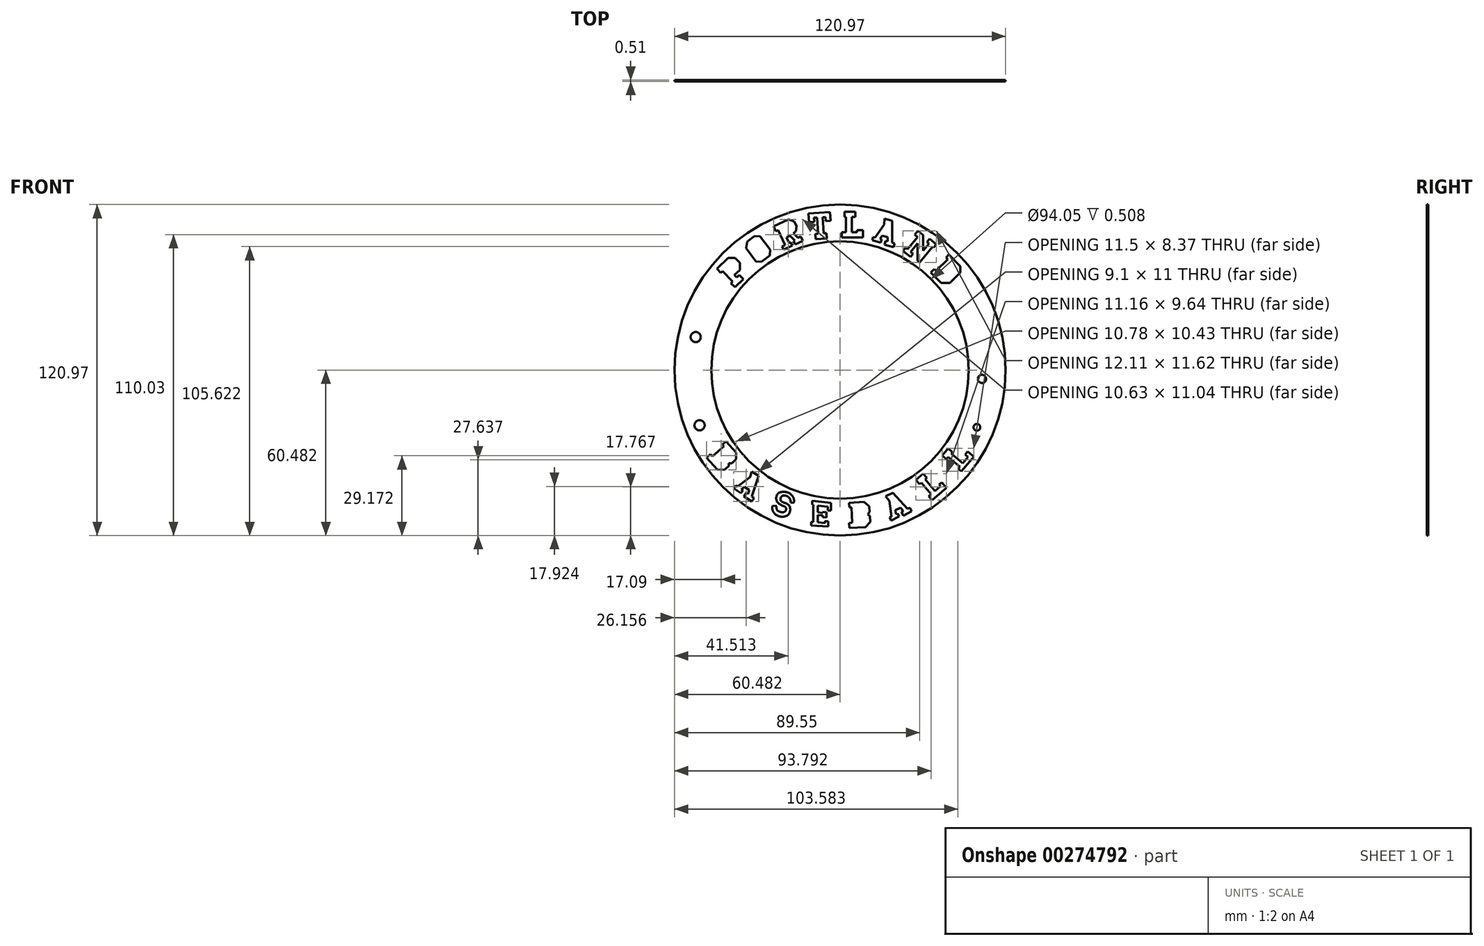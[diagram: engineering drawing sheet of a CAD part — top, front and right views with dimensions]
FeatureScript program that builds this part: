
annotation { "Feature Type Name" : "Feature", "Feature Type Description" : "" }
export const myFeature = defineFeature(function(context is Context, id is Id, definition is map)
    precondition{}
    {
        {
            var Q0;
            Q0=qCreatedBy(makeId("Front.planeOp"),FACE);
            var sketch = newSketch(context, id + "F0", { "sketchPlane" : qUnion([Q0])});
            skLineSegment(sketch, "E0", {"start": v(-46.28, 38.08) * mm, "end": v(-44.82, 36.56) * mm});
            skLineSegment(sketch, "E1", {"start": v(-44.82, 36.56) * mm, "end": v(-44.15, 37.2) * mm});
            skLineSegment(sketch, "E2", {"start": v(-44.15, 37.2) * mm, "end": v(-40.48, 33.42) * mm});
            skLineSegment(sketch, "E3", {"start": v(-40.48, 33.42) * mm, "end": v(-41.1, 32.81) * mm});
            skLineSegment(sketch, "E4", {"start": v(-41.1, 32.81) * mm, "end": v(-39.7, 31.36) * mm});
            skLineSegment(sketch, "E5", {"start": v(-39.7, 31.36) * mm, "end": v(-36.66, 34.3) * mm});
            skLineSegment(sketch, "E6", {"start": v(-36.66, 34.3) * mm, "end": v(-38.08, 35.77) * mm});
            skLineSegment(sketch, "E7", {"start": v(-38.08, 35.77) * mm, "end": v(-38.98, 34.9) * mm});
            skLineSegment(sketch, "E8", {"start": v(-38.98, 34.9) * mm, "end": v(-39.84, 35.8) * mm});
            skLineSegment(sketch, "E9", {"start": v(-39.84, 35.8) * mm, "end": v(-37.93, 37.66) * mm});
            skLineSegment(sketch, "E10", {"start": v(-37.93, 37.66) * mm, "end": v(-37.93, 40.3) * mm});
            skLineSegment(sketch, "E11", {"start": v(-37.93, 40.3) * mm, "end": v(-39.65, 42.08) * mm});
            skLineSegment(sketch, "E12", {"start": v(-46.28, 38.08) * mm, "end": v(-42.2, 42.04) * mm});
            skLineSegment(sketch, "E13", {"start": v(-42.2, 42.04) * mm, "end": v(-39.65, 42.08) * mm});
            skLineSegment(sketch, "E14", {"start": v(-35.23, 47.96) * mm, "end": v(-32.52, 50.01) * mm});
            skLineSegment(sketch, "E15", {"start": v(-32.52, 50.01) * mm, "end": v(-30.46, 49.88) * mm});
            skLineSegment(sketch, "E16", {"start": v(-30.46, 49.88) * mm, "end": v(-26.84, 45.1) * mm});
            skLineSegment(sketch, "E17", {"start": v(-26.84, 45.1) * mm, "end": v(-26.99, 42.91) * mm});
            skLineSegment(sketch, "E18", {"start": v(-26.99, 42.91) * mm, "end": v(-29.94, 40.67) * mm});
            skLineSegment(sketch, "E19", {"start": v(-29.94, 40.67) * mm, "end": v(-31.98, 40.8) * mm});
            skLineSegment(sketch, "E20", {"start": v(-31.98, 40.8) * mm, "end": v(-35.6, 45.6) * mm});
            skLineSegment(sketch, "E21", {"start": v(-35.6, 45.6) * mm, "end": v(-35.23, 47.96) * mm});
            skLineSegment(sketch, "E22", {"start": v(-25.56, 53.6) * mm, "end": v(-20.1, 56.13) * mm});
            skLineSegment(sketch, "E23", {"start": v(-20.1, 56.13) * mm, "end": v(-18.1, 55.45) * mm});
            skLineSegment(sketch, "E24", {"start": v(-18.1, 55.45) * mm, "end": v(-17.14, 53.74) * mm});
            skLineSegment(sketch, "E25", {"start": v(-17.14, 53.74) * mm, "end": v(-17.4, 51.8) * mm});
            skLineSegment(sketch, "E26", {"start": v(-17.4, 51.8) * mm, "end": v(-18.33, 51.12) * mm});
            skLineSegment(sketch, "E27", {"start": v(-18.33, 51.12) * mm, "end": v(-16.65, 49.44) * mm});
            skLineSegment(sketch, "E28", {"start": v(-16.65, 49.44) * mm, "end": v(-15.66, 49.9) * mm});
            skLineSegment(sketch, "E29", {"start": v(-15.66, 49.9) * mm, "end": v(-14.93, 48.34) * mm});
            skLineSegment(sketch, "E30", {"start": v(-14.93, 48.34) * mm, "end": v(-17.73, 47.04) * mm});
            skLineSegment(sketch, "E31", {"start": v(-17.73, 47.04) * mm, "end": v(-18.26, 48.19) * mm});
            skLineSegment(sketch, "E32", {"start": v(-18.26, 48.19) * mm, "end": v(-17.84, 48.38) * mm});
            skLineSegment(sketch, "E33", {"start": v(-17.84, 48.38) * mm, "end": v(-19.58, 50.13) * mm});
            skLineSegment(sketch, "E34", {"start": v(-19.58, 50.13) * mm, "end": v(-20.86, 49.53) * mm});
            skLineSegment(sketch, "E35", {"start": v(-20.86, 49.53) * mm, "end": v(-19.97, 47.61) * mm});
            skLineSegment(sketch, "E36", {"start": v(-19.24, 47.73) * mm, "end": v(-19.88, 47.43) * mm});
            skLineSegment(sketch, "E37", {"start": v(-19.97, 47.61) * mm, "end": v(-19.88, 47.43) * mm});
            skLineSegment(sketch, "E38", {"start": v(-19.24, 47.73) * mm, "end": v(-18.7, 46.58) * mm});
            skLineSegment(sketch, "E39", {"start": v(-18.7, 46.58) * mm, "end": v(-21.91, 45.1) * mm});
            skLineSegment(sketch, "E40", {"start": v(-21.91, 45.1) * mm, "end": v(-22.45, 46.24) * mm});
            skLineSegment(sketch, "E41", {"start": v(-21.35, 46.75) * mm, "end": v(-23.88, 52.19) * mm});
            skLineSegment(sketch, "E42", {"start": v(-23.88, 52.19) * mm, "end": v(-24.72, 51.8) * mm});
            skLineSegment(sketch, "E43.trimOffspring", {"start": v(-21.35, 46.75) * mm, "end": v(-22.45, 46.24) * mm});
            skLineSegment(sketch, "E44", {"start": v(-25.56, 53.6) * mm, "end": v(-24.72, 51.8) * mm});
            skLineSegment(sketch, "E45", {"start": v(-5.45, 58.78) * mm, "end": v(-12.82, 58.3) * mm});
            skLineSegment(sketch, "E46", {"start": v(-12.82, 58.3) * mm, "end": v(-12.6, 55.1) * mm});
            skLineSegment(sketch, "E47", {"start": v(-10.7, 55.23) * mm, "end": v(-10.75, 55.96) * mm});
            skLineSegment(sketch, "E48", {"start": v(-9.68, 56.03) * mm, "end": v(-9.34, 50.88) * mm});
            skLineSegment(sketch, "E49", {"start": v(-9.34, 50.88) * mm, "end": v(-10.33, 50.81) * mm});
            skLineSegment(sketch, "E50", {"start": v(-10.33, 50.81) * mm, "end": v(-10.2, 48.93) * mm});
            skLineSegment(sketch, "E51", {"start": v(-10.2, 48.93) * mm, "end": v(-6.13, 49.2) * mm});
            skLineSegment(sketch, "E52", {"start": v(-7.6, 56.16) * mm, "end": v(-7.26, 51.04) * mm});
            skLineSegment(sketch, "E53", {"start": v(-6.13, 49.2) * mm, "end": v(-6.25, 51.08) * mm});
            skLineSegment(sketch, "E54", {"start": v(-5.45, 58.78) * mm, "end": v(-4.98, 58.8) * mm});
            skLineSegment(sketch, "E55", {"start": v(-4.98, 58.8) * mm, "end": v(-4.77, 55.62) * mm});
            skLineSegment(sketch, "E56.trimOffspring", {"start": v(-6.54, 55.5) * mm, "end": v(-6.59, 56.23) * mm});
            skLineSegment(sketch, "E57", {"start": v(-6.25, 51.08) * mm, "end": v(-7.26, 51.01) * mm});
            skLineSegment(sketch, "E58", {"start": v(-7.26, 51.04) * mm, "end": v(-7.26, 51.01) * mm});
            skLineSegment(sketch, "E59", {"start": v(-10.75, 55.96) * mm, "end": v(-10.8, 56.76) * mm});
            skLineSegment(sketch, "E60", {"start": v(-9.68, 56.03) * mm, "end": v(-9.73, 56.83) * mm});
            skLineSegment(sketch, "E61", {"start": v(-7.6, 56.16) * mm, "end": v(-7.65, 56.97) * mm});
            skLineSegment(sketch, "E62", {"start": v(-6.59, 56.23) * mm, "end": v(-6.64, 57.04) * mm});
            skLineSegment(sketch, "E63", {"start": v(-10.8, 56.76) * mm, "end": v(-9.73, 56.83) * mm});
            skLineSegment(sketch, "E64.trimOffspring", {"start": v(-7.65, 56.97) * mm, "end": v(-6.64, 57.04) * mm});
            skLineSegment(sketch, "E65", {"start": v(-6.54, 55.5) * mm, "end": v(-4.77, 55.62) * mm});
            skLineSegment(sketch, "E66", {"start": v(-10.7, 55.23) * mm, "end": v(-12.6, 55.1) * mm});
            skLineSegment(sketch, "E67", {"start": v(0.4, 59) * mm, "end": v(4.28, 59) * mm});
            skLineSegment(sketch, "E68", {"start": v(4.28, 59) * mm, "end": v(4.28, 56.97) * mm});
            skLineSegment(sketch, "E69", {"start": v(4.28, 56.97) * mm, "end": v(3.06, 56.97) * mm});
            skLineSegment(sketch, "E70", {"start": v(3.06, 56.97) * mm, "end": v(3.06, 51.43) * mm});
            skLineSegment(sketch, "E71", {"start": v(3.06, 51.43) * mm, "end": v(4.97, 51.43) * mm});
            skLineSegment(sketch, "E72", {"start": v(4.97, 51.43) * mm, "end": v(4.97, 52.27) * mm});
            skLineSegment(sketch, "E73", {"start": v(4.97, 52.27) * mm, "end": v(7.04, 52.27) * mm});
            skLineSegment(sketch, "E74", {"start": v(7.04, 52.27) * mm, "end": v(7.04, 49.55) * mm});
            skLineSegment(sketch, "E75", {"start": v(7.04, 49.55) * mm, "end": v(-0.65, 49.55) * mm});
            skLineSegment(sketch, "E76", {"start": v(-0.65, 49.55) * mm, "end": v(-0.65, 51.43) * mm});
            skLineSegment(sketch, "E77", {"start": v(-0.65, 51.43) * mm, "end": v(0.9, 51.43) * mm});
            skLineSegment(sketch, "E78", {"start": v(0.9, 51.43) * mm, "end": v(0.9, 56.97) * mm});
            skLineSegment(sketch, "E79", {"start": v(0.9, 56.97) * mm, "end": v(0.4, 56.97) * mm});
            skLineSegment(sketch, "E80", {"start": v(0.4, 56.97) * mm, "end": v(0.4, 59) * mm});
            skLineSegment(sketch, "E81", {"start": v(14.94, 46.85) * mm, "end": v(18.28, 45.95) * mm});
            skLineSegment(sketch, "E82", {"start": v(18.67, 47.42) * mm, "end": v(17.73, 47.67) * mm});
            skLineSegment(sketch, "E83", {"start": v(17.73, 47.67) * mm, "end": v(17.73, 55.65) * mm});
            skLineSegment(sketch, "E84", {"start": v(14.86, 54.24) * mm, "end": v(11.82, 49.88) * mm});
            skLineSegment(sketch, "E85", {"start": v(16.16, 48.1) * mm, "end": v(15.34, 48.32) * mm});
            skLineSegment(sketch, "E86", {"start": v(14.94, 46.85) * mm, "end": v(15.34, 48.32) * mm});
            skLineSegment(sketch, "E87", {"start": v(10.5, 48.48) * mm, "end": v(13.6, 47.63) * mm});
            skLineSegment(sketch, "E88", {"start": v(13.6, 47.63) * mm, "end": v(13.94, 48.87) * mm});
            skLineSegment(sketch, "E89", {"start": v(13.94, 48.87) * mm, "end": v(13.3, 49.05) * mm});
            skLineSegment(sketch, "E90", {"start": v(11.82, 49.88) * mm, "end": v(11.57, 49.52) * mm});
            skLineSegment(sketch, "E91", {"start": v(13.3, 49.05) * mm, "end": v(13.93, 49.95) * mm});
            skLineSegment(sketch, "E92", {"start": v(16.16, 49.5) * mm, "end": v(16.16, 48.1) * mm});
            skLineSegment(sketch, "E93", {"start": v(14.23, 50.19) * mm, "end": v(16.16, 49.67) * mm});
            skLineSegment(sketch, "E94", {"start": v(16.16, 49.67) * mm, "end": v(16.16, 49.5) * mm});
            skLineSegment(sketch, "E95", {"start": v(13.93, 49.95) * mm, "end": v(14.11, 50.22) * mm});
            skLineSegment(sketch, "E96", {"start": v(14.23, 50.19) * mm, "end": v(14.11, 50.22) * mm});
            skLineSegment(sketch, "E97", {"start": v(17.73, 55.65) * mm, "end": v(14.9, 56.42) * mm});
            skLineSegment(sketch, "E98", {"start": v(14.9, 56.42) * mm, "end": v(14.86, 54.24) * mm});
            skLineSegment(sketch, "E99.trimOffspring", {"start": v(11.57, 49.52) * mm, "end": v(10.83, 49.72) * mm});
            skLineSegment(sketch, "E100", {"start": v(10.83, 49.72) * mm, "end": v(10.5, 48.48) * mm});
            skLineSegment(sketch, "E101", {"start": v(18.67, 47.42) * mm, "end": v(18.28, 45.95) * mm});
            skLineSegment(sketch, "E102", {"start": v(27.17, 52.01) * mm, "end": v(29.03, 50.38) * mm});
            skLineSegment(sketch, "E103", {"start": v(29.03, 50.38) * mm, "end": v(29.03, 44.68) * mm});
            skLineSegment(sketch, "E104", {"start": v(31.47, 49.03) * mm, "end": v(33.85, 46.95) * mm});
            skLineSegment(sketch, "E105", {"start": v(33.85, 46.95) * mm, "end": v(33.04, 46.03) * mm});
            skLineSegment(sketch, "E106", {"start": v(32.5, 46.14) * mm, "end": v(27.83, 40.4) * mm});
            skLineSegment(sketch, "E107", {"start": v(27, 41.06) * mm, "end": v(27, 47.36) * mm});
            skLineSegment(sketch, "E108", {"start": v(27, 47.36) * mm, "end": v(24.78, 44.6) * mm});
            skLineSegment(sketch, "E109", {"start": v(24.78, 44.6) * mm, "end": v(24.5, 44.25) * mm});
            skLineSegment(sketch, "E110", {"start": v(24.5, 44.25) * mm, "end": v(25.4, 43.52) * mm});
            skLineSegment(sketch, "E111", {"start": v(24.48, 42.4) * mm, "end": v(21.73, 44.63) * mm});
            skLineSegment(sketch, "E112", {"start": v(25.4, 43.52) * mm, "end": v(24.48, 42.4) * mm});
            skLineSegment(sketch, "E113", {"start": v(31.47, 49.03) * mm, "end": v(30.66, 48.1) * mm});
            skLineSegment(sketch, "E114", {"start": v(30.48, 47.9) * mm, "end": v(31.25, 47.22) * mm});
            skLineSegment(sketch, "E115", {"start": v(30.66, 48.1) * mm, "end": v(30.48, 47.9) * mm});
            skLineSegment(sketch, "E116", {"start": v(33.04, 46.03) * mm, "end": v(32.85, 45.82) * mm});
            skLineSegment(sketch, "E117", {"start": v(29.03, 44.68) * mm, "end": v(31.25, 47.22) * mm});
            skLineSegment(sketch, "E118.trimOffspring", {"start": v(32.5, 46.14) * mm, "end": v(32.85, 45.82) * mm});
            skLineSegment(sketch, "E119", {"start": v(27.17, 52.01) * mm, "end": v(25.99, 50.56) * mm});
            skLineSegment(sketch, "E120", {"start": v(23.34, 45.19) * mm, "end": v(22.65, 45.75) * mm});
            skLineSegment(sketch, "E121", {"start": v(21.73, 44.63) * mm, "end": v(22.65, 45.75) * mm});
            skLineSegment(sketch, "E122", {"start": v(23.34, 45.19) * mm, "end": v(26.7, 49.32) * mm});
            skLineSegment(sketch, "E123", {"start": v(26.7, 49.32) * mm, "end": v(27.02, 49.72) * mm});
            skLineSegment(sketch, "E124", {"start": v(27.02, 49.72) * mm, "end": v(25.99, 50.56) * mm});
            skLineSegment(sketch, "E125", {"start": v(27, 41.06) * mm, "end": v(27.83, 40.4) * mm});
            skLineSegment(sketch, "E126", {"start": v(38.52, 43.26) * mm, "end": v(42.64, 39.06) * mm});
            skLineSegment(sketch, "E127", {"start": v(42.64, 39.06) * mm, "end": v(42.64, 36.66) * mm});
            skLineSegment(sketch, "E128", {"start": v(42.64, 36.66) * mm, "end": v(38.83, 32.88) * mm});
            skLineSegment(sketch, "E129", {"start": v(38.83, 32.88) * mm, "end": v(35.68, 32.88) * mm});
            skLineSegment(sketch, "E130", {"start": v(35.68, 32.88) * mm, "end": v(31.88, 36.76) * mm});
            skLineSegment(sketch, "E131", {"start": v(38.52, 43.26) * mm, "end": v(37.4, 42.16) * mm});
            skLineSegment(sketch, "E132", {"start": v(37.4, 42.16) * mm, "end": v(38.02, 41.52) * mm});
            skLineSegment(sketch, "E133", {"start": v(38.02, 41.52) * mm, "end": v(33.8, 37.39) * mm});
            skLineSegment(sketch, "E134", {"start": v(33.8, 37.39) * mm, "end": v(33.17, 38.03) * mm});
            skLineSegment(sketch, "E135.trimOffspring", {"start": v(33.17, 38.03) * mm, "end": v(31.88, 36.76) * mm});
            skLineSegment(sketch, "E136", {"start": v(-50.06, -30.95) * mm, "end": v(-48.68, -29.7) * mm});
            skLineSegment(sketch, "E137", {"start": v(-48.68, -29.7) * mm, "end": v(-47.92, -30.52) * mm});
            skLineSegment(sketch, "E138", {"start": v(-47.92, -30.52) * mm, "end": v(-43.76, -26.72) * mm});
            skLineSegment(sketch, "E139", {"start": v(-43.76, -26.72) * mm, "end": v(-44.24, -26.2) * mm});
            skLineSegment(sketch, "E140", {"start": v(-44.24, -26.2) * mm, "end": v(-42.95, -25.03) * mm});
            skLineSegment(sketch, "E141", {"start": v(-42.95, -25.03) * mm, "end": v(-39.28, -29.06) * mm});
            skLineSegment(sketch, "E142", {"start": v(-39.28, -29.06) * mm, "end": v(-39.28, -31.54) * mm});
            skLineSegment(sketch, "E143", {"start": v(-39.28, -31.54) * mm, "end": v(-40.84, -32.97) * mm});
            skLineSegment(sketch, "E144", {"start": v(-40.84, -32.97) * mm, "end": v(-41.96, -32.97) * mm});
            skLineSegment(sketch, "E145", {"start": v(-41.96, -32.97) * mm, "end": v(-41.96, -34) * mm});
            skLineSegment(sketch, "E146", {"start": v(-41.96, -34) * mm, "end": v(-43.58, -35.46) * mm});
            skLineSegment(sketch, "E147", {"start": v(-50.06, -30.95) * mm, "end": v(-46.08, -35.31) * mm});
            skLineSegment(sketch, "E148", {"start": v(-46.08, -35.31) * mm, "end": v(-43.58, -35.46) * mm});
            skLineSegment(sketch, "E149", {"start": v(-36.42, -45.1) * mm, "end": v(-33.53, -47) * mm});
            skLineSegment(sketch, "E150", {"start": v(-32.7, -45.72) * mm, "end": v(-33.52, -45.19) * mm});
            skLineSegment(sketch, "E151", {"start": v(-33.52, -45.19) * mm, "end": v(-31.06, -37.6) * mm});
            skLineSegment(sketch, "E152", {"start": v(-34.22, -38.06) * mm, "end": v(-38.45, -41.26) * mm});
            skLineSegment(sketch, "E153", {"start": v(-34.88, -44.3) * mm, "end": v(-35.59, -43.83) * mm});
            skLineSegment(sketch, "E154", {"start": v(-36.42, -45.1) * mm, "end": v(-35.59, -43.83) * mm});
            skLineSegment(sketch, "E155", {"start": v(-40.15, -42.19) * mm, "end": v(-37.45, -43.95) * mm});
            skLineSegment(sketch, "E156", {"start": v(-37.45, -43.95) * mm, "end": v(-36.75, -42.88) * mm});
            skLineSegment(sketch, "E157", {"start": v(-36.75, -42.88) * mm, "end": v(-37.31, -42.5) * mm});
            skLineSegment(sketch, "E158", {"start": v(-38.45, -41.26) * mm, "end": v(-38.8, -41.53) * mm});
            skLineSegment(sketch, "E159", {"start": v(-37.31, -42.5) * mm, "end": v(-36.43, -41.84) * mm});
            skLineSegment(sketch, "E160", {"start": v(-34.45, -42.96) * mm, "end": v(-34.88, -44.3) * mm});
            skLineSegment(sketch, "E161", {"start": v(-36.07, -41.71) * mm, "end": v(-34.4, -42.8) * mm});
            skLineSegment(sketch, "E162", {"start": v(-36.43, -41.84) * mm, "end": v(-36.17, -41.64) * mm});
            skLineSegment(sketch, "E163", {"start": v(-36.07, -41.71) * mm, "end": v(-36.17, -41.64) * mm});
            skLineSegment(sketch, "E164", {"start": v(-31.06, -37.6) * mm, "end": v(-33.5, -36) * mm});
            skLineSegment(sketch, "E165", {"start": v(-33.5, -36) * mm, "end": v(-34.22, -38.06) * mm});
            skLineSegment(sketch, "E166.trimOffspring", {"start": v(-38.8, -41.53) * mm, "end": v(-39.45, -41.11) * mm});
            skLineSegment(sketch, "E167", {"start": v(-39.45, -41.11) * mm, "end": v(-40.15, -42.19) * mm});
            skLineSegment(sketch, "E168", {"start": v(-32.7, -45.72) * mm, "end": v(-33.53, -47) * mm});
            skLineSegment(sketch, "E169", {"start": v(21.82, -52.15) * mm, "end": v(24.9, -50.58) * mm});
            skLineSegment(sketch, "E170", {"start": v(24.2, -49.23) * mm, "end": v(23.33, -49.67) * mm});
            skLineSegment(sketch, "E171", {"start": v(23.33, -49.67) * mm, "end": v(17.98, -43.76) * mm});
            skLineSegment(sketch, "E172", {"start": v(16.8, -46.73) * mm, "end": v(17.47, -52) * mm});
            skLineSegment(sketch, "E173", {"start": v(21.88, -50.4) * mm, "end": v(21.13, -50.8) * mm});
            skLineSegment(sketch, "E174", {"start": v(21.82, -52.15) * mm, "end": v(21.13, -50.8) * mm});
            skLineSegment(sketch, "E175", {"start": v(17.43, -53.93) * mm, "end": v(20.3, -52.47) * mm});
            skLineSegment(sketch, "E176", {"start": v(20.3, -52.47) * mm, "end": v(19.72, -51.32) * mm});
            skLineSegment(sketch, "E177", {"start": v(19.72, -51.32) * mm, "end": v(19.12, -51.63) * mm});
            skLineSegment(sketch, "E178", {"start": v(17.47, -52) * mm, "end": v(17.53, -52.44) * mm});
            skLineSegment(sketch, "E179", {"start": v(19.12, -51.63) * mm, "end": v(18.98, -50.53) * mm});
            skLineSegment(sketch, "E180", {"start": v(20.94, -49.37) * mm, "end": v(21.88, -50.4) * mm});
            skLineSegment(sketch, "E181", {"start": v(19.05, -50.15) * mm, "end": v(20.83, -49.25) * mm});
            skLineSegment(sketch, "E182", {"start": v(20.83, -49.25) * mm, "end": v(20.94, -49.37) * mm});
            skLineSegment(sketch, "E183", {"start": v(18.98, -50.53) * mm, "end": v(18.94, -50.2) * mm});
            skLineSegment(sketch, "E184", {"start": v(19.05, -50.15) * mm, "end": v(18.94, -50.2) * mm});
            skLineSegment(sketch, "E185", {"start": v(17.98, -43.76) * mm, "end": v(15.37, -45.08) * mm});
            skLineSegment(sketch, "E186", {"start": v(15.37, -45.08) * mm, "end": v(16.8, -46.73) * mm});
            skLineSegment(sketch, "E187.trimOffspring", {"start": v(17.53, -52.44) * mm, "end": v(16.84, -52.78) * mm});
            skLineSegment(sketch, "E188", {"start": v(16.84, -52.78) * mm, "end": v(17.43, -53.93) * mm});
            skLineSegment(sketch, "E189", {"start": v(24.2, -49.23) * mm, "end": v(24.9, -50.58) * mm});
            skLineSegment(sketch, "E190.0", {"start": v(20.94, -49.37) * mm, "end": v(20.83, -49.25) * mm, "construction": true});
            skLineSegment(sketch, "E191", {"start": v(26.45, -39.06) * mm, "end": v(29.1, -36.83) * mm});
            skLineSegment(sketch, "E192", {"start": v(30.4, -38.38) * mm, "end": v(29.79, -38.9) * mm});
            skLineSegment(sketch, "E193", {"start": v(29.79, -38.9) * mm, "end": v(33.35, -43.15) * mm});
            skLineSegment(sketch, "E194", {"start": v(33.35, -43.15) * mm, "end": v(34.82, -41.91) * mm});
            skLineSegment(sketch, "E195", {"start": v(34.85, -40.8) * mm, "end": v(35.86, -39.94) * mm});
            skLineSegment(sketch, "E196", {"start": v(35.86, -39.94) * mm, "end": v(37.61, -42.03) * mm});
            skLineSegment(sketch, "E197", {"start": v(37.61, -42.03) * mm, "end": v(32.31, -46.47) * mm});
            skLineSegment(sketch, "E198", {"start": v(31.1, -45.03) * mm, "end": v(31.7, -44.53) * mm});
            skLineSegment(sketch, "E199", {"start": v(28.14, -40.29) * mm, "end": v(27.75, -40.6) * mm});
            skLineSegment(sketch, "E200", {"start": v(27.75, -40.6) * mm, "end": v(26.45, -39.06) * mm});
            skLineSegment(sketch, "E201.0", {"start": v(28.14, -40.29) * mm, "end": v(29.79, -38.9) * mm, "construction": true});
            skLineSegment(sketch, "E202.0", {"start": v(31.1, -45.03) * mm, "end": v(34.82, -41.91) * mm, "construction": true});
            skLineSegment(sketch, "E203.0", {"start": v(27.75, -40.6) * mm, "end": v(26.45, -39.06) * mm, "construction": true});
            skLineSegment(sketch, "E204", {"start": v(36.08, -30.19) * mm, "end": v(38.25, -27.6) * mm});
            skLineSegment(sketch, "E205", {"start": v(39.8, -28.9) * mm, "end": v(39.33, -29.46) * mm});
            skLineSegment(sketch, "E206", {"start": v(39.33, -29.46) * mm, "end": v(43.58, -33.02) * mm});
            skLineSegment(sketch, "E207", {"start": v(43.58, -33.02) * mm, "end": v(44.82, -31.55) * mm});
            skLineSegment(sketch, "E208", {"start": v(41.9, -35.01) * mm, "end": v(42.2, -34.67) * mm});
            skLineSegment(sketch, "E209", {"start": v(37.95, -31.1) * mm, "end": v(37.63, -31.5) * mm});
            skLineSegment(sketch, "E210", {"start": v(37.63, -31.5) * mm, "end": v(36.08, -30.19) * mm});
            skLineSegment(sketch, "E211.0", {"start": v(37.95, -31.1) * mm, "end": v(39.33, -29.46) * mm, "construction": true});
            skLineSegment(sketch, "E212.0", {"start": v(42.2, -34.67) * mm, "end": v(44.82, -31.55) * mm, "construction": true});
            skLineSegment(sketch, "E213.0", {"start": v(37.63, -31.5) * mm, "end": v(36.08, -30.19) * mm, "construction": true});
            skLineSegment(sketch, "E214", {"start": v(44.82, -31.55) * mm, "end": v(45.5, -30.74) * mm});
            skLineSegment(sketch, "E215", {"start": v(45.5, -30.74) * mm, "end": v(44.43, -29.85) * mm});
            skLineSegment(sketch, "E216", {"start": v(44.43, -29.85) * mm, "end": v(45.37, -28.73) * mm});
            skLineSegment(sketch, "E217", {"start": v(45.37, -28.73) * mm, "end": v(47.57, -30.57) * mm});
            skLineSegment(sketch, "E218", {"start": v(47.57, -30.57) * mm, "end": v(43.04, -35.97) * mm});
            skLineSegment(sketch, "E219", {"start": v(43.04, -35.97) * mm, "end": v(41.9, -35.01) * mm});
            skLineSegment(sketch, "E220", {"start": v(39.8, -28.9) * mm, "end": v(38.25, -27.6) * mm});
            skLineSegment(sketch, "E221", {"start": v(42.2, -34.67) * mm, "end": v(42.48, -34.33) * mm});
            skLineSegment(sketch, "E222", {"start": v(42.48, -34.33) * mm, "end": v(38.24, -30.76) * mm});
            skLineSegment(sketch, "E223", {"start": v(38.24, -30.76) * mm, "end": v(37.95, -31.1) * mm});
            skLineSegment(sketch, "E224", {"start": v(29.1, -36.83) * mm, "end": v(30.4, -38.38) * mm});
            skLineSegment(sketch, "E225", {"start": v(31.1, -45.03) * mm, "end": v(32.31, -46.47) * mm});
            skLineSegment(sketch, "E226", {"start": v(34.82, -41.91) * mm, "end": v(35.4, -41.44) * mm});
            skLineSegment(sketch, "E227", {"start": v(35.4, -41.44) * mm, "end": v(34.85, -40.8) * mm});
            skLineSegment(sketch, "E228", {"start": v(28.14, -40.29) * mm, "end": v(28.4, -40.06) * mm});
            skLineSegment(sketch, "E229", {"start": v(28.4, -40.06) * mm, "end": v(31.97, -44.31) * mm});
            skLineSegment(sketch, "E230", {"start": v(31.97, -44.31) * mm, "end": v(31.7, -44.53) * mm});
            skLineSegment(sketch, "E231", {"start": v(2.12, -56.68) * mm, "end": v(2.02, -54.82) * mm});
            skLineSegment(sketch, "E232", {"start": v(2.02, -54.82) * mm, "end": v(3.14, -54.76) * mm});
            skLineSegment(sketch, "E233", {"start": v(3.14, -54.76) * mm, "end": v(2.84, -49.13) * mm});
            skLineSegment(sketch, "E234", {"start": v(2.84, -49.13) * mm, "end": v(2.14, -49.17) * mm});
            skLineSegment(sketch, "E235", {"start": v(2.14, -49.17) * mm, "end": v(2.04, -47.43) * mm});
            skLineSegment(sketch, "E236", {"start": v(2.04, -47.43) * mm, "end": v(7.49, -47.14) * mm});
            skLineSegment(sketch, "E237", {"start": v(7.49, -47.14) * mm, "end": v(9.4, -48.72) * mm});
            skLineSegment(sketch, "E238", {"start": v(9.4, -48.72) * mm, "end": v(9.52, -50.83) * mm});
            skLineSegment(sketch, "E239", {"start": v(9.52, -50.83) * mm, "end": v(8.81, -51.7) * mm});
            skLineSegment(sketch, "E240", {"start": v(8.81, -51.7) * mm, "end": v(9.6, -52.35) * mm});
            skLineSegment(sketch, "E241", {"start": v(9.6, -52.35) * mm, "end": v(9.72, -54.53) * mm});
            skLineSegment(sketch, "E242", {"start": v(2.12, -56.68) * mm, "end": v(8.02, -56.37) * mm});
            skLineSegment(sketch, "E243", {"start": v(8.02, -56.37) * mm, "end": v(9.72, -54.53) * mm});
            skArc(sketch, "E244", {"start": v(-18.21, -47.48) * mm, "mid": v(-18.16, -46.03) * mm, "end": v(-18.83, -44.74) * mm});
            skArc(sketch, "E245", {"start": v(-18.83, -44.74) * mm, "mid": v(-21.06, -43.51) * mm, "end": v(-23.58, -43.83) * mm});
            skArc(sketch, "E246", {"start": v(-23.58, -43.83) * mm, "mid": v(-24.58, -45.32) * mm, "end": v(-24.25, -47.08) * mm});
            skArc(sketch, "E247", {"start": v(-24.25, -47.08) * mm, "mid": v(-23.22, -48.06) * mm, "end": v(-21.93, -48.66) * mm});
            skArc(sketch, "E248", {"start": v(-21.78, -50.84) * mm, "mid": v(-20.97, -49.7) * mm, "end": v(-21.93, -48.66) * mm});
            skArc(sketch, "E249", {"start": v(-24.25, -50.19) * mm, "mid": v(-23.1, -50.8) * mm, "end": v(-21.78, -50.84) * mm});
            skArc(sketch, "E250", {"start": v(-24.46, -48.66) * mm, "mid": v(-24.48, -49.44) * mm, "end": v(-24.25, -50.19) * mm});
            skLineSegment(sketch, "E251", {"start": v(-24.46, -48.66) * mm, "end": v(-25.94, -48.52) * mm});
            skArc(sketch, "E252", {"start": v(-25.94, -48.52) * mm, "mid": v(-25.9, -50.17) * mm, "end": v(-25.06, -51.58) * mm});
            skArc(sketch, "E253", {"start": v(-25.06, -51.58) * mm, "mid": v(-22.85, -52.53) * mm, "end": v(-20.5, -52.05) * mm});
            skArc(sketch, "E254", {"start": v(-20.5, -52.05) * mm, "mid": v(-19.54, -50.4) * mm, "end": v(-19.83, -48.52) * mm});
            skLineSegment(sketch, "E255", {"start": v(-18.21, -47.48) * mm, "end": v(-19.35, -47.37) * mm});
            skArc(sketch, "E256", {"start": v(-19.35, -47.37) * mm, "mid": v(-20.13, -45.36) * mm, "end": v(-22.22, -44.86) * mm});
            skArc(sketch, "E257", {"start": v(-22.22, -44.86) * mm, "mid": v(-22.98, -45.66) * mm, "end": v(-22.84, -46.74) * mm});
            skArc(sketch, "E258", {"start": v(-19.83, -48.52) * mm, "mid": v(-20.63, -47.85) * mm, "end": v(-21.59, -47.45) * mm});
            skArc(sketch, "E259", {"start": v(-22.84, -46.74) * mm, "mid": v(-22.27, -47.2) * mm, "end": v(-21.59, -47.45) * mm});
            skLineSegment(sketch, "E260", {"start": v(-11.41, -46.8) * mm, "end": v(-4.86, -47.43) * mm});
            skLineSegment(sketch, "E261", {"start": v(-4.86, -47.43) * mm, "end": v(-4.6, -47.46) * mm});
            skLineSegment(sketch, "E262", {"start": v(-4.6, -47.46) * mm, "end": v(-4.6, -50.32) * mm});
            skLineSegment(sketch, "E263", {"start": v(-4.6, -50.32) * mm, "end": v(-5.74, -50.32) * mm});
            skLineSegment(sketch, "E264", {"start": v(-5.74, -50.32) * mm, "end": v(-5.74, -48.89) * mm});
            skLineSegment(sketch, "E265", {"start": v(-5.74, -48.89) * mm, "end": v(-9.36, -48.53) * mm});
            skLineSegment(sketch, "E266", {"start": v(-9.36, -48.53) * mm, "end": v(-9.36, -50.96) * mm});
            skLineSegment(sketch, "E267", {"start": v(-9.36, -50.96) * mm, "end": v(-7.58, -51.14) * mm});
            skLineSegment(sketch, "E268", {"start": v(-7.58, -51.14) * mm, "end": v(-7.58, -50.75) * mm});
            skLineSegment(sketch, "E269", {"start": v(-7.58, -50.75) * mm, "end": v(-6.3, -50.87) * mm});
            skLineSegment(sketch, "E270", {"start": v(-6.3, -50.87) * mm, "end": v(-6.3, -52.8) * mm});
            skLineSegment(sketch, "E271", {"start": v(-6.3, -52.8) * mm, "end": v(-7.58, -52.67) * mm});
            skLineSegment(sketch, "E272", {"start": v(-7.58, -52.67) * mm, "end": v(-7.58, -52.11) * mm});
            skLineSegment(sketch, "E273", {"start": v(-7.58, -52.11) * mm, "end": v(-9.36, -51.94) * mm});
            skLineSegment(sketch, "E274", {"start": v(-9.36, -51.94) * mm, "end": v(-9.36, -54.63) * mm});
            skLineSegment(sketch, "E275", {"start": v(-6.79, -54.8) * mm, "end": v(-6.76, -54.04) * mm});
            skLineSegment(sketch, "E276", {"start": v(-6.76, -54.04) * mm, "end": v(-5.57, -54.16) * mm});
            skLineSegment(sketch, "E277", {"start": v(-5.57, -54.16) * mm, "end": v(-5.57, -56.17) * mm});
            skLineSegment(sketch, "E278", {"start": v(-5.57, -56.17) * mm, "end": v(-11.83, -55.76) * mm});
            skLineSegment(sketch, "E279", {"start": v(-11, -54.52) * mm, "end": v(-11, -48.12) * mm});
            skLineSegment(sketch, "E280", {"start": v(-11, -48.12) * mm, "end": v(-11.47, -48.07) * mm});
            skLineSegment(sketch, "E281", {"start": v(-11.47, -48.07) * mm, "end": v(-11.47, -46.79) * mm});
            skLineSegment(sketch, "E282", {"start": v(-11.41, -46.8) * mm, "end": v(-11.47, -46.79) * mm});
            skLineSegment(sketch, "E283", {"start": v(-11.83, -54.47) * mm, "end": v(-11, -54.52) * mm});
            skLineSegment(sketch, "E284.trimOffspring", {"start": v(-9.36, -54.63) * mm, "end": v(-6.79, -54.8) * mm});
            skLineSegment(sketch, "E285", {"start": v(-11.83, -54.47) * mm, "end": v(-11.83, -55.76) * mm});
            skLineSegment(sketch, "E286", {"start": v(-34.45, -42.96) * mm, "end": v(-34.4, -42.8) * mm});
            skCircle(sketch, "E287", {"center": v(-52.6, -19.12) * mm, "radius": 1.86 * mm});
            skCircle(sketch, "E288", {"center": v(-54, 13.11) * mm, "radius": 1.86 * mm});
            skCircle(sketch, "E289", {"center": v(48.71, -19.85) * mm, "radius": 1.23 * mm});
            skCircle(sketch, "E290", {"center": v(50.57, -2.17) * mm, "radius": 1.5 * mm});
            skCircle(sketch, "E291", {"center": v(-1.28, 1.06) * mm, "radius": 47.02 * mm});
            skCircle(sketch, "E292", {"center": v(-1.28, 1.06) * mm, "radius": 60.48 * mm});
            skSolve(sketch);
        }
        {
            var Q0;
            Q0=makeQuery(id+"F0.imprint","IMPRINT",FACE,{"disambiguationData":[TD([[makeQuery(id+"F0.imprint","IMPRINT",EDGE,{"derivedFrom":sQuery(id+"F0.wireOp",EDGE,"E0")}),-1.0]])]});
            extrude(context, id + "F1", {"entities" : qUnion([Q0]), "depth" : 0.5 * mm});
        }
    });
